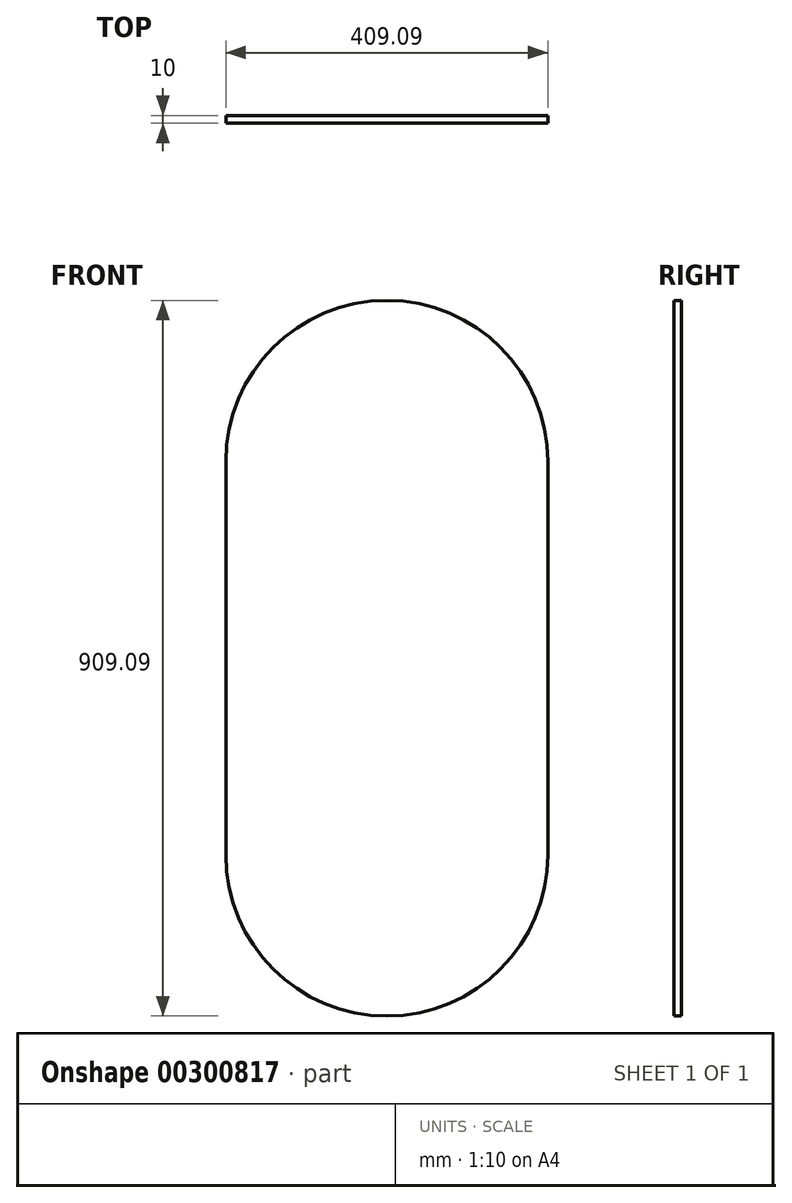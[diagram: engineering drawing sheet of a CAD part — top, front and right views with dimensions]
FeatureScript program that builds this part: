
annotation { "Feature Type Name" : "Feature", "Feature Type Description" : "" }
export const myFeature = defineFeature(function(context is Context, id is Id, definition is map)
    precondition{}
    {
        {
            var Q0;
            Q0=qCreatedBy(makeId("Front.planeOp"),FACE);
            var sketch = newSketch(context, id + "F0", { "sketchPlane" : qUnion([Q0])});
            skLineSegment(sketch, "E0.left", {"start": v(0, -699.13) * mm, "end": v(0, 300.87) * mm});
            skLineSegment(sketch, "E0.right", {"start": v(818.18, -699.13) * mm, "end": v(818.18, 300.87) * mm});
            skArc(sketch, "E1", {"start": v(818.18, -699.13) * mm, "mid": v(409.1, -1108.23) * mm, "end": v(0, -699.13) * mm});
            skArc(sketch, "E2", {"start": v(0, 300.87) * mm, "mid": v(409.1, 709.96) * mm, "end": v(818.18, 300.87) * mm});
            skSolve(sketch);
        }
        {
            var Q0;
            Q0=qSketchRegion(id+"F0",true);
            extrude(context, id + "F1", {"entities" : qUnion([Q0]), "depth" : 20 * mm});
        }
        {
            var Q0;
            Q0=makeQuery(id+"F1.opExtrude","SWEPT_BODY",BODY,{"disambiguationData":[OSD([sQuery(id+"F0.wireOp",EDGE,"E0.left"),sQuery(id+"F0.wireOp",EDGE,"E0.right"),sQuery(id+"F0.wireOp",EDGE,"E1"),sQuery(id+"F0.wireOp",EDGE,"E2")])]});
            var Q1;
            Q1=qCreatedBy(makeId("Origin.pointOp"),VERTEX);
            var Q2;
            Q2=qCreatedBy(makeId("Origin.pointOp"),VERTEX);
            transform(context, id + "F2", {"entities" : qUnion([Q0]), "transformType" : TransformType.SCALE_UNIFORMLY, "scale" : 0.5, "scalePoint" : qUnion([Q2]), "makeCopy" : false});
        }
    });
